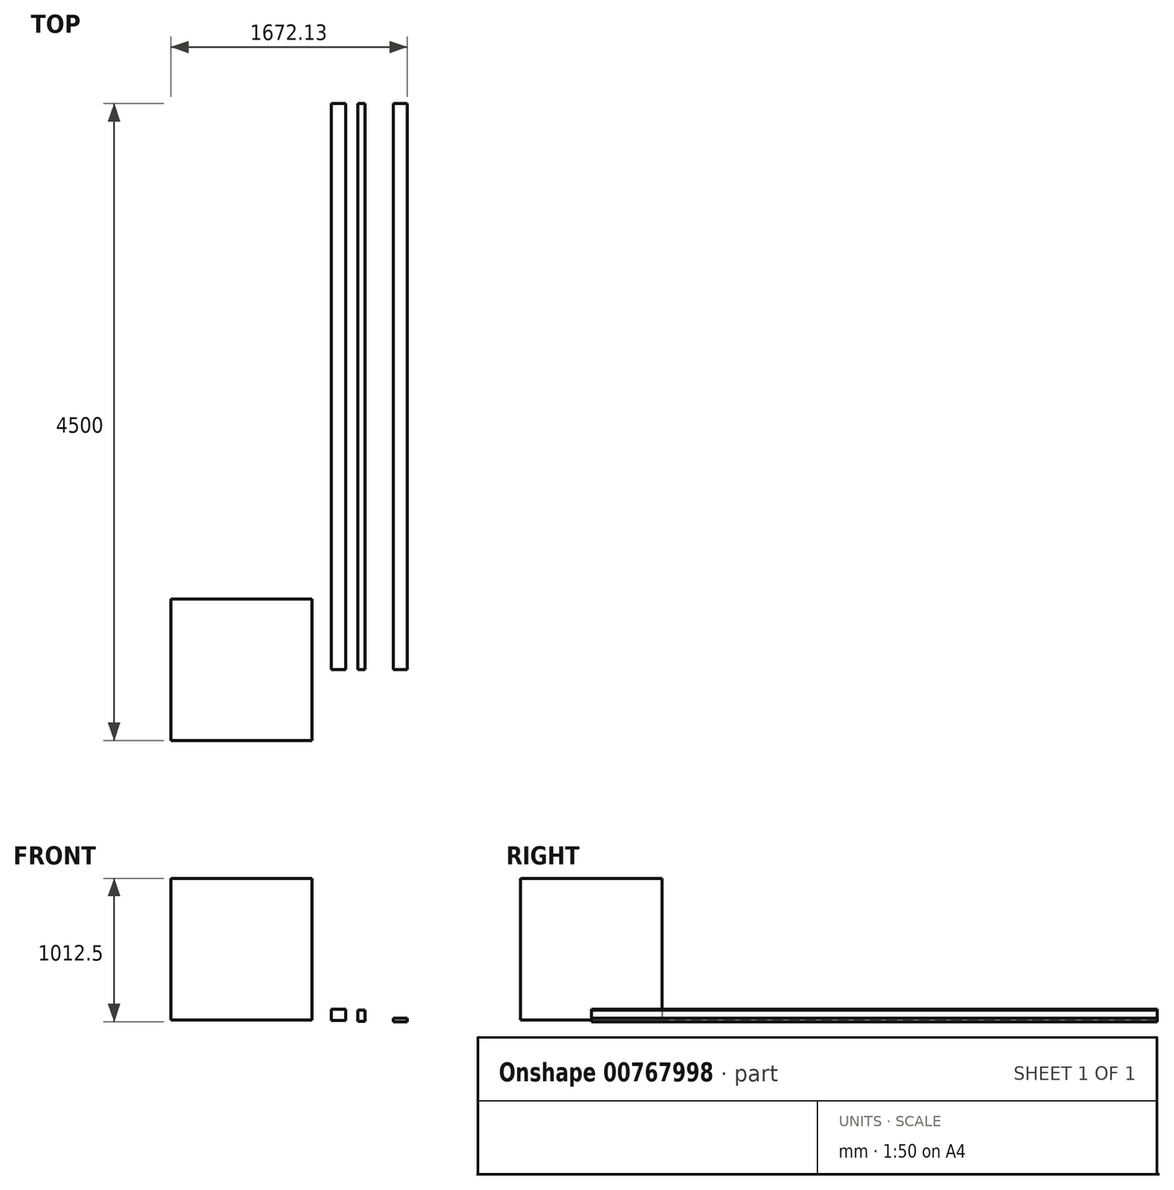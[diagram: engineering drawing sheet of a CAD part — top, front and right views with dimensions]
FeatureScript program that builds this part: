
annotation { "Feature Type Name" : "Feature", "Feature Type Description" : "" }
export const myFeature = defineFeature(function(context is Context, id is Id, definition is map)
    precondition{}
    {
        {
            var Q0;
            Q0=qCreatedBy(makeId("Top.planeOp"),FACE);
            var sketch = newSketch(context, id + "F0", { "sketchPlane" : qUnion([Q0])});
            skLineSegment(sketch, "E0.bottom", {"start": v(500, -500) * mm, "end": v(-500, -500) * mm});
            skLineSegment(sketch, "E0.top", {"start": v(500, 500) * mm, "end": v(-500, 500) * mm});
            skLineSegment(sketch, "E0.left", {"start": v(500, -500) * mm, "end": v(500, 500) * mm});
            skLineSegment(sketch, "E0.right", {"start": v(-500, -500) * mm, "end": v(-500, 500) * mm});
            skPoint(sketch, "E0.middle", {"position": v(0, 0) * mm});
            skSolve(sketch);
        }
        {
            var Q0;
            Q0=makeQuery(id+"F0.imprint","IMPRINT",FACE,{"disambiguationData":[TD([[makeQuery(id+"F0.imprint","IMPRINT",EDGE,{"derivedFrom":sQuery(id+"F0.wireOp",EDGE,"E0.bottom")}),-1.0]])]});
            extrude(context, id + "F1", {"entities" : qUnion([Q0]), "depth" : 1000 * mm, "offsetDistance" : 25 * mm});
        }
        {
            var Q0;
            Q0=qCreatedBy(makeId("Front.planeOp"),FACE);
            var sketch = newSketch(context, id + "F2", { "sketchPlane" : qUnion([Q0])});
            skLineSegment(sketch, "E1.bottom", {"start": v(736.34, 75.93) * mm, "end": v(636.34, 75.93) * mm});
            skLineSegment(sketch, "E1.top", {"start": v(736.34, -4.07) * mm, "end": v(636.34, -4.07) * mm});
            skLineSegment(sketch, "E1.left", {"start": v(736.34, 75.93) * mm, "end": v(736.34, -4.07) * mm});
            skLineSegment(sketch, "E1.right", {"start": v(636.34, 75.93) * mm, "end": v(636.34, -4.07) * mm});
            skPoint(sketch, "E1.middle", {"position": v(686.34, 35.93) * mm});
            skLineSegment(sketch, "E2.bottom", {"start": v(873.88, 69.84) * mm, "end": v(823.88, 69.84) * mm});
            skLineSegment(sketch, "E2.top", {"start": v(873.88, -10.16) * mm, "end": v(823.88, -10.16) * mm});
            skLineSegment(sketch, "E2.left", {"start": v(873.88, 69.84) * mm, "end": v(873.88, -10.16) * mm});
            skLineSegment(sketch, "E2.right", {"start": v(823.88, 69.84) * mm, "end": v(823.88, -10.16) * mm});
            skPoint(sketch, "E2.middle", {"position": v(848.88, 29.84) * mm});
            skLineSegment(sketch, "E3.bottom", {"start": v(1172.13, 12.5) * mm, "end": v(1072.13, 12.5) * mm});
            skLineSegment(sketch, "E3.top", {"start": v(1172.13, -12.5) * mm, "end": v(1072.13, -12.5) * mm});
            skLineSegment(sketch, "E3.left", {"start": v(1172.13, 12.5) * mm, "end": v(1172.13, -12.5) * mm});
            skLineSegment(sketch, "E3.right", {"start": v(1072.13, 12.5) * mm, "end": v(1072.13, -12.5) * mm});
            skPoint(sketch, "E3.middle", {"position": v(1122.13, 0) * mm});
            skLineSegment(sketch, "E4.bottom", {"start": v(1395.8, 76.15) * mm, "end": v(1309.66, 76.15) * mm});
            skLineSegment(sketch, "E4.top", {"start": v(1395.8, 2.3) * mm, "end": v(1309.66, 2.3) * mm});
            skLineSegment(sketch, "E4.left", {"start": v(1395.8, 76.15) * mm, "end": v(1395.8, 2.3) * mm});
            skLineSegment(sketch, "E4.right", {"start": v(1309.66, 76.15) * mm, "end": v(1309.66, 2.3) * mm});
            skPoint(sketch, "E4.middle", {"position": v(1352.73, 39.23) * mm});
            skLineSegment(sketch, "E5.bottom", {"start": v(1626.38, 67) * mm, "end": v(1478.75, 67) * mm});
            skLineSegment(sketch, "E5.top", {"start": v(1626.38, -67) * mm, "end": v(1478.75, -67) * mm});
            skLineSegment(sketch, "E5.left", {"start": v(1626.38, 67) * mm, "end": v(1626.38, -67) * mm});
            skLineSegment(sketch, "E5.right", {"start": v(1478.75, 67) * mm, "end": v(1478.75, -67) * mm});
            skPoint(sketch, "E5.middle", {"position": v(1552.56, 0) * mm});
            skSolve(sketch);
        }
        {
            var Q0;
            Q0=makeQuery(id+"F2.imprint","IMPRINT",FACE,{"disambiguationData":[TD([[makeQuery(id+"F2.imprint","IMPRINT",EDGE,{"derivedFrom":sQuery(id+"F2.wireOp",EDGE,"E1.bottom")}),1.0]])]});
            var Q1;
            Q1=makeQuery(id+"F2.imprint","IMPRINT",FACE,{"disambiguationData":[TD([[makeQuery(id+"F2.imprint","IMPRINT",EDGE,{"derivedFrom":sQuery(id+"F2.wireOp",EDGE,"E2.bottom")}),1.0]])]});
            var Q2;
            Q2=makeQuery(id+"F2.imprint","IMPRINT",FACE,{"disambiguationData":[TD([[makeQuery(id+"F2.imprint","IMPRINT",EDGE,{"derivedFrom":sQuery(id+"F2.wireOp",EDGE,"E3.bottom")}),1.0]])]});
            extrude(context, id + "F3", {"entities" : qUnion([Q0, Q1, Q2]), "oppositeDirection" : true, "depth" : 4000 * mm, "offsetDistance" : 25 * mm});
        }
    });
